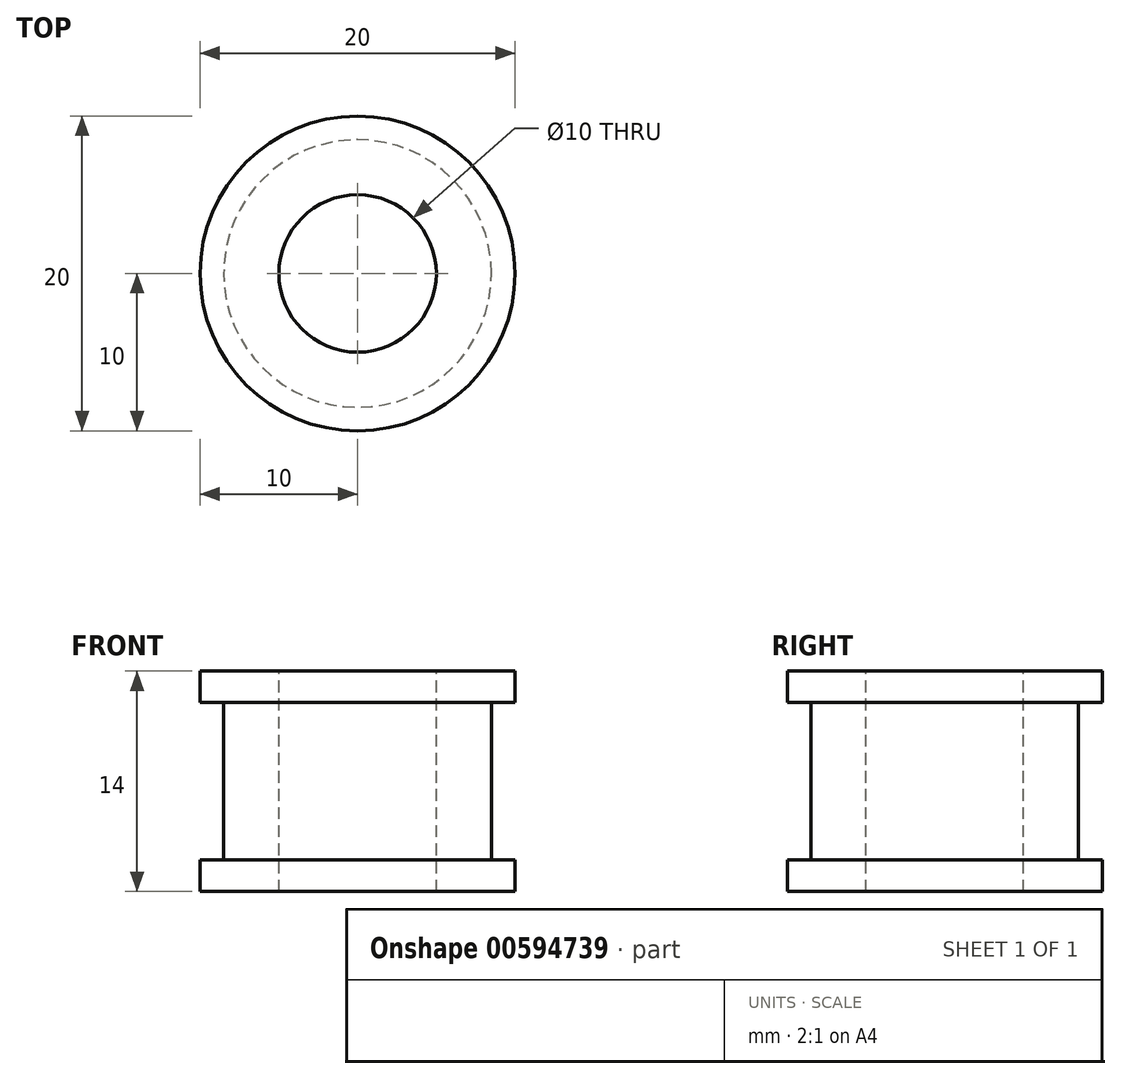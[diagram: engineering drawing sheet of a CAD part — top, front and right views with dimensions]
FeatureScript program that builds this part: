
annotation { "Feature Type Name" : "Feature", "Feature Type Description" : "" }
export const myFeature = defineFeature(function(context is Context, id is Id, definition is map)
    precondition{}
    {
        {
            var Q0;
            Q0=qCreatedBy(makeId("Top.planeOp"),FACE);
            var sketch = newSketch(context, id + "F0", { "sketchPlane" : qUnion([Q0])});
            skCircle(sketch, "E0", {"center": v(0, 0) * mm, "radius": 10 * mm});
            skSolve(sketch);
        }
        {
            var Q0;
            Q0 = qSketchRegion(id + "F0", true);
            extrude(context, id + "F1", {"entities" : qUnion([Q0]), "depth" : 2 * mm, "offsetDistance" : 25 * mm});
        }
        {
            var Q0;
            Q0=makeQuery(id+"F1.opExtrude","CAP_FACE",FACE,{"disambiguationData":[OSD([sQuery(id+"F0.wireOp",EDGE,"E0")])],"isStart":false});
            var sketch = newSketch(context, id + "F2", { "sketchPlane" : qUnion([Q0])});
            skCircle(sketch, "E1", {"center": v(0, 0) * mm, "radius": 8.5 * mm});
            skSolve(sketch);
        }
        {
            var Q0;
            Q0 = qSketchRegion(id + "F2", true);
            extrude(context, id + "F3", {"entities" : qUnion([Q0]), "operationType" : NewBodyOperationType.ADD, "depth" : 10 * mm, "offsetDistance" : 25 * mm});
        }
        {
            var Q0;
            Q0=makeQuery(id+"F3.opExtrude","CAP_FACE",FACE,{"disambiguationData":[OSD([sQuery(id+"F2.wireOp",EDGE,"E1")])],"isStart":false});
            var sketch = newSketch(context, id + "F4", { "sketchPlane" : qUnion([Q0])});
            skCircle(sketch, "E2", {"center": v(0, 0) * mm, "radius": 10 * mm});
            skSolve(sketch);
        }
        {
            var Q0;
            Q0 = qSketchRegion(id + "F4", true);
            extrude(context, id + "F5", {"entities" : qUnion([Q0]), "operationType" : NewBodyOperationType.ADD, "depth" : 2 * mm, "offsetDistance" : 25 * mm});
        }
        {
            var Q0;
            Q0=makeQuery(id+"F5.opExtrude","CAP_FACE",FACE,{"disambiguationData":[OSD([sQuery(id+"F4.wireOp",EDGE,"E2")])],"isStart":false});
            var sketch = newSketch(context, id + "F6", { "sketchPlane" : qUnion([Q0])});
            skCircle(sketch, "E3", {"center": v(0, 0) * mm, "radius": 5 * mm});
            skSolve(sketch);
        }
        {
            var Q0;
            Q0 = qSketchRegion(id + "F6", true);
            extrude(context, id + "F7", {"entities" : qUnion([Q0]), "operationType" : NewBodyOperationType.REMOVE, "oppositeDirection" : true, "depth" : 20 * mm, "offsetDistance" : 25 * mm, "hasSecondDirection" : true, "secondDirectionOppositeDirection" : false, "secondDirectionDepth" : 6 * mm});
        }
    });
